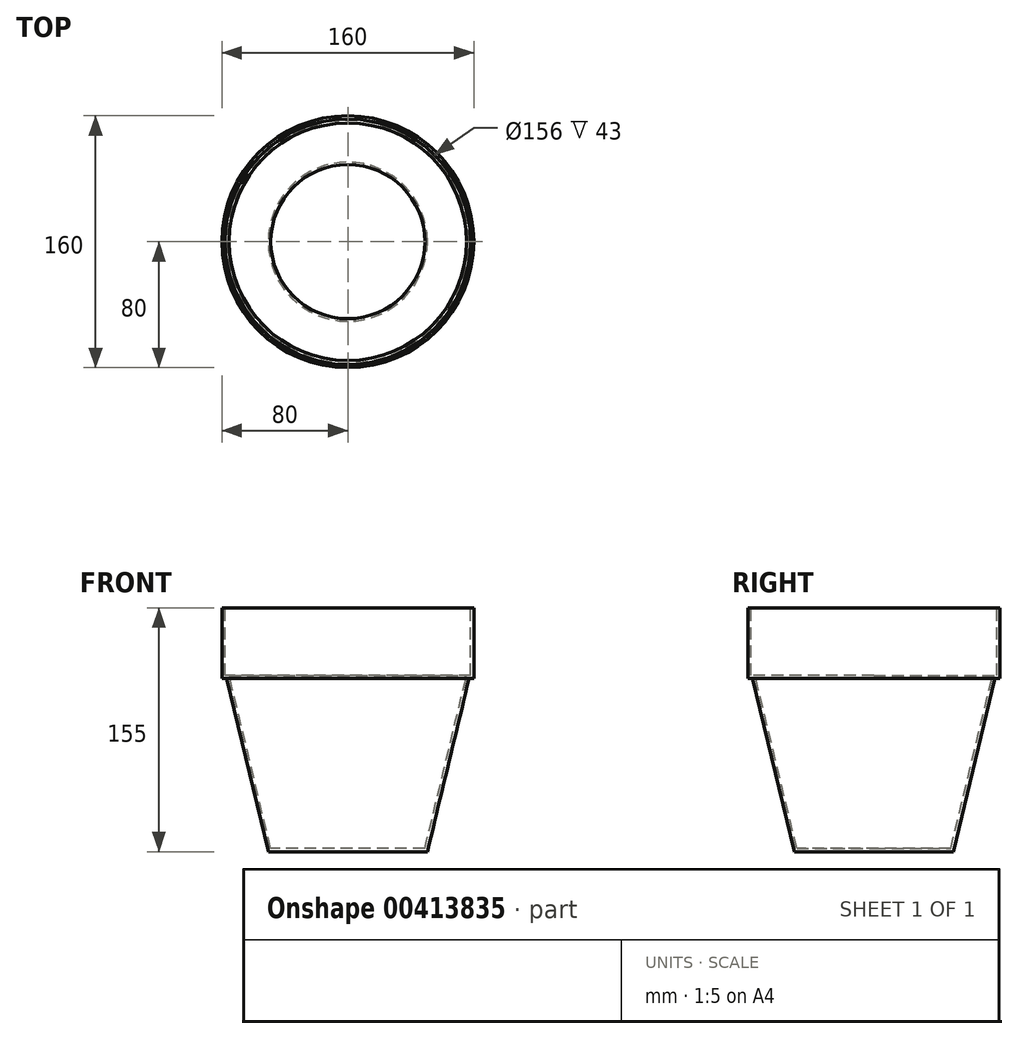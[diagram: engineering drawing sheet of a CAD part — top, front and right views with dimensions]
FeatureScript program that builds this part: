
annotation { "Feature Type Name" : "Feature", "Feature Type Description" : "" }
export const myFeature = defineFeature(function(context is Context, id is Id, definition is map)
    precondition{}
    {
        {
            var Q0;
            Q0=qCreatedBy(makeId("Front.planeOp"),FACE);
            var sketch = newSketch(context, id + "F0", { "sketchPlane" : qUnion([Q0])});
            skLineSegment(sketch, "E0", {"start": v(0, 63.42) * mm, "end": v(-80, 63.42) * mm});
            skLineSegment(sketch, "E1", {"start": v(-80, 63.42) * mm, "end": v(-80, 18.42) * mm});
            skLineSegment(sketch, "E2", {"start": v(0, -91.58) * mm, "end": v(-50.5, -91.58) * mm});
            skLineSegment(sketch, "E3", {"start": v(-80, 18.42) * mm, "end": v(-77, 18.42) * mm});
            skLineSegment(sketch, "E4", {"start": v(0, 63.42) * mm, "end": v(0, -91.58) * mm});
            skLineSegment(sketch, "E5", {"start": v(-77, 18.42) * mm, "end": v(-50.5, -91.58) * mm});
            skLineSegment(sketch, "E6.MirrorCS", {"start": v(0, 63.42) * mm, "end": v(80, 63.42) * mm});
            skLineSegment(sketch, "E7.MirrorCS", {"start": v(80, 63.42) * mm, "end": v(80, 18.42) * mm});
            skLineSegment(sketch, "E8.MirrorCS", {"start": v(80, 18.42) * mm, "end": v(77, 18.42) * mm});
            skLineSegment(sketch, "E9.MirrorCS", {"start": v(77, 18.42) * mm, "end": v(50.5, -91.58) * mm});
            skLineSegment(sketch, "E10.MirrorCS", {"start": v(0, -91.58) * mm, "end": v(50.5, -91.58) * mm});
            skSolve(sketch);
        }
        {
            var Q0;
            {var subQ0=sQuery(id+"F0.wireOp",EDGE,"E3");Q0=makeQuery(id+"F0.imprint","IMPRINT",FACE,{"disambiguationData":[TD([[makeQuery(id+"F0.imprint","IMPRINT",EDGE,{"derivedFrom":subQ0}),1.0]])]});}
            var Q1;
            {var subQ1=sQuery(id+"F0.wireOp",EDGE,"E0");Q1=makeQuery(id+"F0.imprint","IMPRINT",FACE,{"disambiguationData":[TD([[makeQuery(id+"F0.imprint","IMPRINT",EDGE,{"derivedFrom":subQ1}),1.0]])]});}
            var Q2;
            Q2=makeQuery(id+"F0.imprint","IMPRINT",FACE,{"disambiguationData":[TD([[makeQuery(id+"F0.imprint","IMPRINT",EDGE,{"derivedFrom":sQuery(id+"F0.wireOp",EDGE,"Kfnrekvc-ZjTY-c2iQ-cK4z-hKnBe4uEAVNk")}),1.0]])]});
            var Q3;
            Q3=sQuery(id+"F0.wireOp",EDGE,"E4");
            revolve(context, id + "F1", {"surfaceOperationType" : NewSurfaceOperationType.NEW, "entities" : qUnion([Q0, Q1, Q2]), "axis" : qUnion([Q3]), "revolveType" : RevolveType.ONE_DIRECTION, "angle" : 360 * degree});
        }
        {
            var Q0;
            Q0=makeQuery(id+"FK2OT3XlAi37Aaq_1.splitOp","SPLIT",FACE,{"derivedFrom":makeQuery(id+"F1.opRevolve","SWEPT_FACE",FACE,{"disambiguationData":[OSD([sQuery(id+"F0.wireOp",EDGE,"E0")])]}),"isFromBackBody":true});
            shell(context, id + "F2", {"entities" : qUnion([Q0]), "thickness" : 2 * mm});
        }
    });
